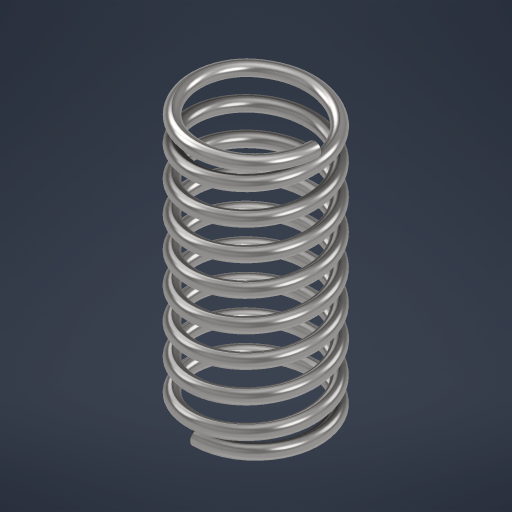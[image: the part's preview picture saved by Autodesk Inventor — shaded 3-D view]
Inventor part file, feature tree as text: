
AUTODESK INVENTOR PART (.ipt)
format: ipt  version: 2024.1 (Build 281209000, 209)  size: 816,128 bytes
history: native  units: mm
features: helix x1
ambient origin geometry x8: Origin, YZ Plane, XZ Plane, XY Plane, X Axis, Y Axis, Z Axis, Center Point
bodies: Body1 (feature_tree)
feature tree (1):
  helix  "Coil2"  [1 undecoded]
note: 1 required parameter value undecoded (feature->parameter linkage not recoverable at this tier; creation-order binding heuristic only, values carry confidence <= 0.55)
